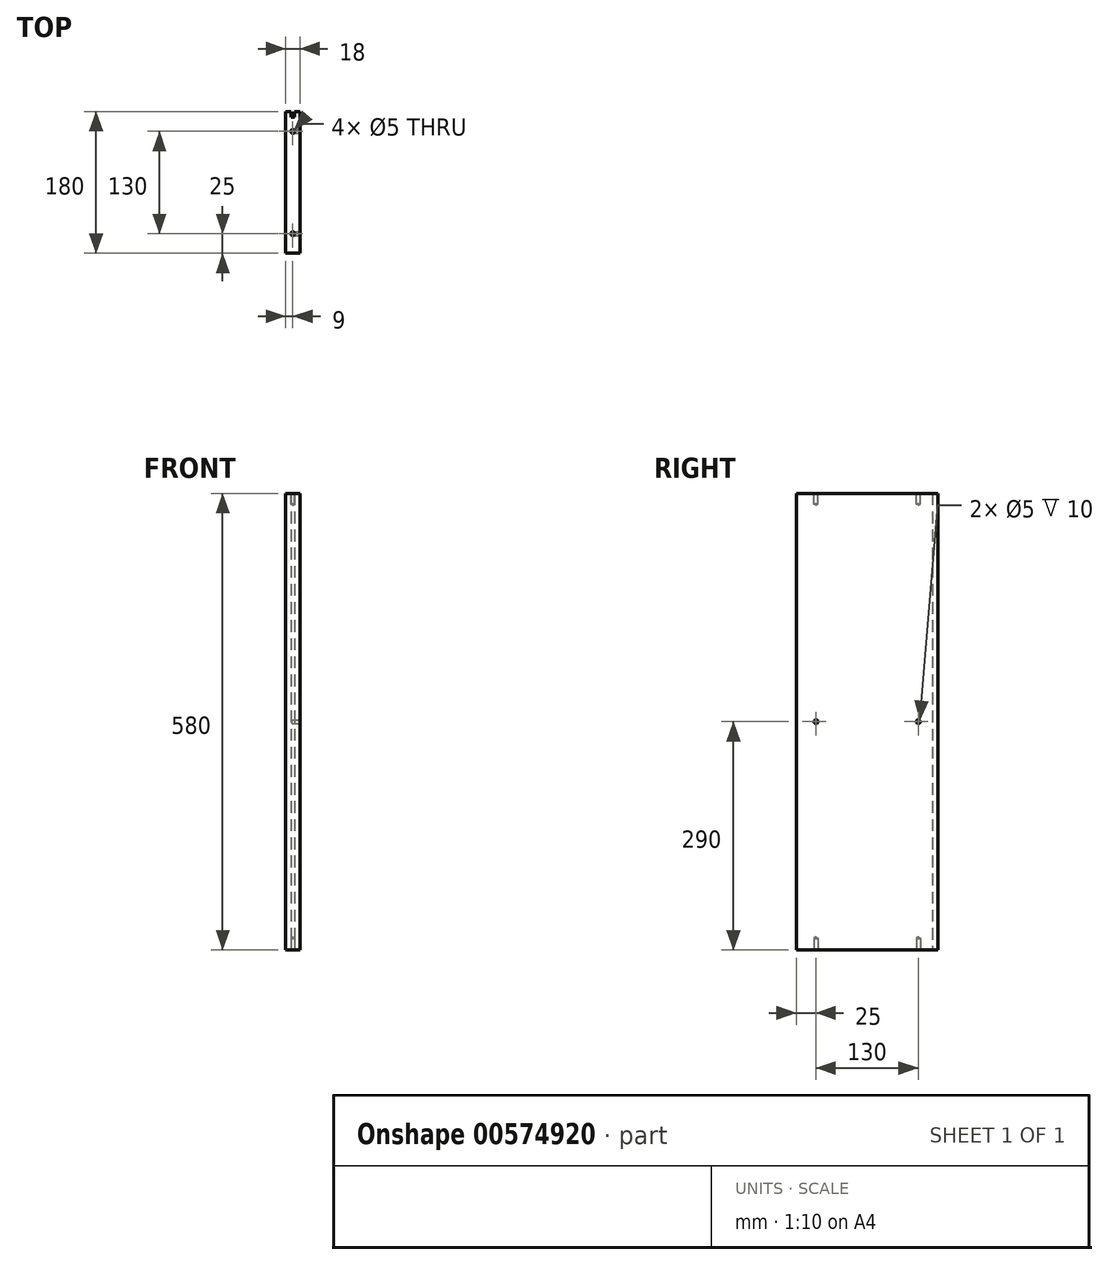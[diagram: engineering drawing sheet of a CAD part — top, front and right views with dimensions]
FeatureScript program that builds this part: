
annotation { "Feature Type Name" : "Feature", "Feature Type Description" : "" }
export const myFeature = defineFeature(function(context is Context, id is Id, definition is map)
    precondition{}
    {
        {
            var Q0;
            Q0=qCreatedBy(makeId("Front.planeOp"),FACE);
            var sketch = newSketch(context, id + "F0", { "sketchPlane" : qUnion([Q0])});
            skLineSegment(sketch, "E0.bottom", {"start": v(9, 290) * mm, "end": v(-9, 290) * mm});
            skLineSegment(sketch, "E0.top", {"start": v(9, -290) * mm, "end": v(-9, -290) * mm});
            skLineSegment(sketch, "E0.left", {"start": v(9, 290) * mm, "end": v(9, -290) * mm});
            skLineSegment(sketch, "E0.right", {"start": v(-9, 290) * mm, "end": v(-9, -290) * mm});
            skPoint(sketch, "E0.middle", {"position": v(0, 0) * mm});
            skSolve(sketch);
        }
        {
            var Q0;
            Q0=qSketchRegion(id+"F0",true);
            extrude(context, id + "F1", {"entities" : qUnion([Q0]), "depth" : 180 * mm, "offsetDistance" : 25 * mm, "symmetric" : true});
        }
        {
            var Q0;
            Q0=makeQuery(id+"F1.opExtrude","SWEPT_FACE",FACE,{"disambiguationData":[OSD([sQuery(id+"F0.wireOp",EDGE,"E0.bottom")])]});
            var sketch = newSketch(context, id + "F2", { "sketchPlane" : qUnion([Q0])});
            skPoint(sketch, "E1", {"position": v(0, -65) * mm});
            skPoint(sketch, "E2", {"position": v(0, 65) * mm});
            skSolve(sketch);
        }
        {
            var Q0;
            Q0=sQuery(id+"F2.wireOp",VERTEX,"E2");
            var Q1;
            Q1=sQuery(id+"F2.wireOp",VERTEX,"E1");
            var Q2;
            Q2=makeQuery(id+"F1.opExtrude","SWEPT_BODY",BODY,{"disambiguationData":[OSD([sQuery(id+"F0.wireOp",EDGE,"E0.bottom"),sQuery(id+"F0.wireOp",EDGE,"E0.top"),sQuery(id+"F0.wireOp",EDGE,"E0.left"),sQuery(id+"F0.wireOp",EDGE,"E0.right")])]});
            hole(context, id + "F3", {"style" : HoleStyle.SIMPLE, "endStyle" : HoleEndStyle.BLIND, "holeDiameter" : 5 * mm, "holeDepth" : 13.5 * mm, "isTappedThrough" : true, "tappedDepth" : 12 * mm, "tapClearance" : 3, "locations" : qUnion([Q0, Q1]), "scope" : qUnion([Q2])});
        }
        {
            var Q0;
            Q0=makeQuery(id+"F1.opExtrude","SWEPT_FACE",FACE,{"disambiguationData":[OSD([sQuery(id+"F0.wireOp",EDGE,"E0.top")])]});
            var sketch = newSketch(context, id + "F4", { "sketchPlane" : qUnion([Q0])});
            skPoint(sketch, "E3", {"position": v(0, 65) * mm});
            skPoint(sketch, "E4", {"position": v(0, -65) * mm});
            skSolve(sketch);
        }
        {
            var Q0;
            Q0=sQuery(id+"F4.wireOp",VERTEX,"E3");
            var Q1;
            Q1=sQuery(id+"F4.wireOp",VERTEX,"E4");
            var Q2;
            Q2=makeQuery(id+"F1.opExtrude","SWEPT_BODY",BODY,{"disambiguationData":[OSD([sQuery(id+"F0.wireOp",EDGE,"E0.bottom"),sQuery(id+"F0.wireOp",EDGE,"E0.top"),sQuery(id+"F0.wireOp",EDGE,"E0.left"),sQuery(id+"F0.wireOp",EDGE,"E0.right")])]});
            hole(context, id + "F5", {"style" : HoleStyle.SIMPLE, "endStyle" : HoleEndStyle.BLIND, "holeDiameter" : 5 * mm, "holeDepth" : 15 * mm, "isTappedThrough" : true, "tappedDepth" : 12 * mm, "tapClearance" : 3, "locations" : qUnion([Q0, Q1]), "scope" : qUnion([Q2])});
        }
        {
            var Q0;
            Q0=makeQuery(id+"F1.opExtrude","SWEPT_FACE",FACE,{"disambiguationData":[OSD([sQuery(id+"F0.wireOp",EDGE,"E0.left")])]});
            var sketch = newSketch(context, id + "F6", { "sketchPlane" : qUnion([Q0])});
            skCircle(sketch, "E5", {"center": v(-60, 0) * mm, "radius": 2.5 * mm});
            skCircle(sketch, "E6", {"center": v(60, 0) * mm, "radius": 2.5 * mm});
            skSolve(sketch);
        }
        {
            var Q0;
            Q0=makeQuery(id+"F6.imprint","IMPRINT",FACE,{"disambiguationData":[TD([[makeQuery(id+"F6.imprint","IMPRINT",EDGE,{"derivedFrom":sQuery(id+"F6.wireOp",EDGE,"E5")}),-1.0]])]});
            extrude(context, id + "F7", {"entities" : qUnion([Q0]), "operationType" : NewBodyOperationType.REMOVE, "depth" : 10 * mm, "offsetDistance" : 25 * mm});
        }
        {
            var Q0;
            Q0=makeQuery(id+"F1.opExtrude","SWEPT_FACE",FACE,{"disambiguationData":[OSD([sQuery(id+"F0.wireOp",EDGE,"E0.left")])]});
            var sketch = newSketch(context, id + "F8", { "sketchPlane" : qUnion([Q0])});
            skCircle(sketch, "E7", {"center": v(-65, 0) * mm, "radius": 2.5 * mm});
            skCircle(sketch, "E8", {"center": v(65, 0) * mm, "radius": 2.5 * mm});
            skSolve(sketch);
        }
        {
            var Q0;
            Q0=qSketchRegion(id+"F8",true);
            extrude(context, id + "F9", {"entities" : qUnion([Q0]), "operationType" : NewBodyOperationType.REMOVE, "oppositeDirection" : true, "depth" : 10 * mm, "offsetDistance" : 25 * mm});
        }
        {
            var Q0;
            Q0=makeQuery(id+"F1.opExtrude","CAP_FACE",FACE,{"disambiguationData":[OSD([sQuery(id+"F0.wireOp",EDGE,"E0.bottom"),sQuery(id+"F0.wireOp",EDGE,"E0.top"),sQuery(id+"F0.wireOp",EDGE,"E0.left"),sQuery(id+"F0.wireOp",EDGE,"E0.right")])],"isStart":true});
            var sketch = newSketch(context, id + "F10", { "sketchPlane" : qUnion([Q0])});
            skLineSegment(sketch, "E9.bottom", {"start": v(2, 290) * mm, "end": v(-2, 290) * mm});
            skLineSegment(sketch, "E9.top", {"start": v(2, -290) * mm, "end": v(-2, -290) * mm});
            skLineSegment(sketch, "E9.left", {"start": v(2, 290) * mm, "end": v(2, -290) * mm});
            skLineSegment(sketch, "E9.right", {"start": v(-2, 290) * mm, "end": v(-2, -290) * mm});
            skSolve(sketch);
        }
        {
            var Q0;
            Q0 = qSketchRegion(id + "F10", true);
            extrude(context, id + "F11", {"entities" : qUnion([Q0]), "operationType" : NewBodyOperationType.REMOVE, "oppositeDirection" : true, "depth" : 7 * mm, "offsetDistance" : 25 * mm});
        }
    });
